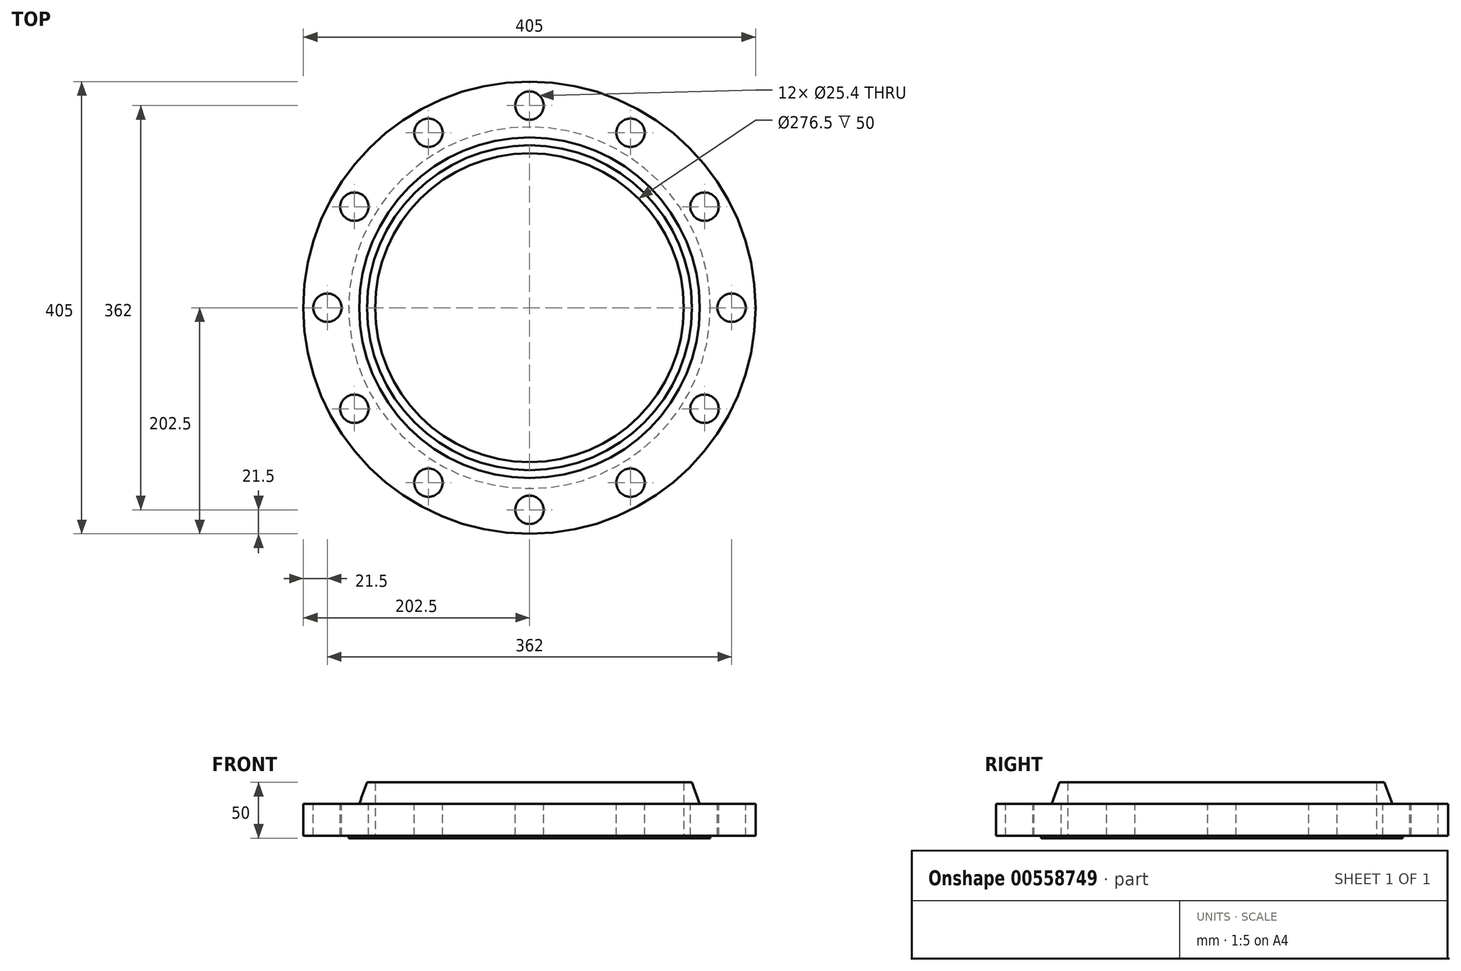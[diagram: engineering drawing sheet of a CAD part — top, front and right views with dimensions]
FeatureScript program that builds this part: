
annotation { "Feature Type Name" : "Feature", "Feature Type Description" : "" }
export const myFeature = defineFeature(function(context is Context, id is Id, definition is map)
    precondition{}
    {
        {
            var Q0;
            Q0=qCreatedBy(makeId("Front.planeOp"),FACE);
            var sketch = newSketch(context, id + "F0", { "sketchPlane" : qUnion([Q0])});
            skLineSegment(sketch, "E0", {"start": v(138.25, 0) * mm, "end": v(161.9, 0) * mm});
            skLineSegment(sketch, "E1", {"start": v(161.9, 0) * mm, "end": v(161.9, 2) * mm});
            skLineSegment(sketch, "E2", {"start": v(161.9, 2) * mm, "end": v(202.5, 2) * mm});
            skLineSegment(sketch, "E3", {"start": v(202.5, 2) * mm, "end": v(202.5, 30.6) * mm});
            skLineSegment(sketch, "E4", {"start": v(202.5, 30.6) * mm, "end": v(152.5, 30.6) * mm});
            skLineSegment(sketch, "E5", {"start": v(152.5, 30.6) * mm, "end": v(145.44, 50) * mm});
            skLineSegment(sketch, "E6", {"start": v(145.44, 50) * mm, "end": v(138.25, 50) * mm});
            skLineSegment(sketch, "E7", {"start": v(138.25, 50) * mm, "end": v(138.25, 0) * mm});
            skLineSegment(sketch, "E8", {"start": v(0, 0) * mm, "end": v(0, 50) * mm});
            skSolve(sketch);
        }
        {
            var Q0;
            Q0=makeQuery(id+"F0.imprint","IMPRINT",FACE,{"disambiguationData":[TD([[makeQuery(id+"F0.imprint","IMPRINT",EDGE,{"derivedFrom":sQuery(id+"F0.wireOp",EDGE,"E0")}),1.0]])]});
            var Q1;
            Q1=sQuery(id+"F0.wireOp",EDGE,"E8");
            revolve(context, id + "F1", {"entities" : qUnion([Q0]), "axis" : qUnion([Q1]), "revolveType" : RevolveType.FULL});
        }
        {
            var Q0;
            Q0=makeQuery(id+"F1.opRevolve","SWEPT_FACE",FACE,{"disambiguationData":[OSD([sQuery(id+"F0.wireOp",EDGE,"E4")])]});
            var sketch = newSketch(context, id + "F2", { "sketchPlane" : qUnion([Q0])});
            skCircle(sketch, "E9", {"center": v(0, 0) * mm, "radius": 181 * mm, "construction": true});
            skCircle(sketch, "E10", {"center": v(0, 181) * mm, "radius": 12.7 * mm});
            skCircle(sketch, "E11.1.0", {"center": v(-90.5, 156.75) * mm, "radius": 12.7 * mm});
            skCircle(sketch, "E11.2.0", {"center": v(-156.75, 90.5) * mm, "radius": 12.7 * mm});
            skCircle(sketch, "E11.3.0", {"center": v(-181, 0) * mm, "radius": 12.7 * mm});
            skCircle(sketch, "E11.4.0", {"center": v(-156.75, -90.5) * mm, "radius": 12.7 * mm});
            skCircle(sketch, "E11.5.0", {"center": v(-90.5, -156.75) * mm, "radius": 12.7 * mm});
            skCircle(sketch, "E11.6.0", {"center": v(0, -181) * mm, "radius": 12.7 * mm});
            skCircle(sketch, "E11.7.0", {"center": v(90.5, -156.75) * mm, "radius": 12.7 * mm});
            skCircle(sketch, "E11.8.0", {"center": v(156.75, -90.5) * mm, "radius": 12.7 * mm});
            skCircle(sketch, "E11.9.0", {"center": v(181, 0) * mm, "radius": 12.7 * mm});
            skCircle(sketch, "E11.10.0", {"center": v(156.75, 90.5) * mm, "radius": 12.7 * mm});
            skCircle(sketch, "E11.11.0", {"center": v(90.5, 156.75) * mm, "radius": 12.7 * mm});
            skSolve(sketch);
        }
        {
            var Q0;
            Q0=qSketchRegion(id+"F2",true);
            extrude(context, id + "F3", {"entities" : qUnion([Q0]), "operationType" : NewBodyOperationType.REMOVE, "endBound" : BoundingType.THROUGH_ALL, "oppositeDirection" : true, "depth" : 25 * mm, "offsetDistance" : 25 * mm});
        }
    });
